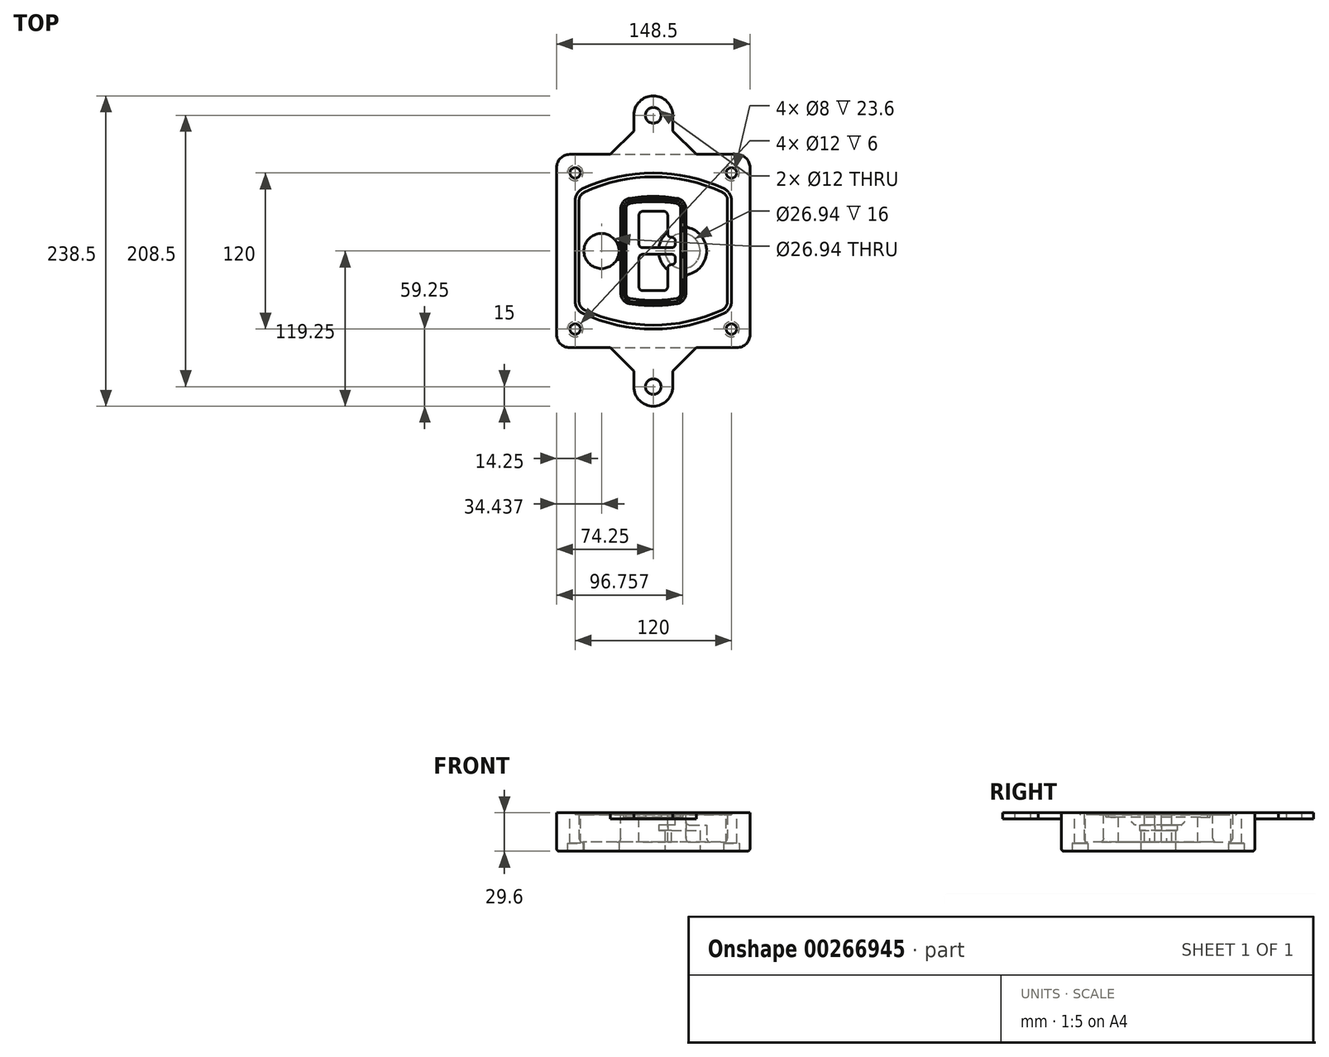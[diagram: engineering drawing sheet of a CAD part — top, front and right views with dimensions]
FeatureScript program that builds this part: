
annotation { "Feature Type Name" : "Feature", "Feature Type Description" : "" }
export const myFeature = defineFeature(function(context is Context, id is Id, definition is map)
    precondition{}
    {
        {
            var Q0;
            Q0=qCreatedBy(makeId("Top.planeOp"),FACE);
            var sketch = newSketch(context, id + "F0", { "sketchPlane" : qUnion([Q0])});
            skPoint(sketch, "E0.rect.middle", {"position": v(0, 0) * mm});
            skLineSegment(sketch, "E1.bottom", {"start": v(-64.25, -74.25) * mm, "end": v(64.25, -74.25) * mm});
            skLineSegment(sketch, "E1.top", {"start": v(-64.25, 74.25) * mm, "end": v(64.25, 74.25) * mm});
            skLineSegment(sketch, "E1.left", {"start": v(-74.25, -64.25) * mm, "end": v(-74.25, 64.25) * mm});
            skLineSegment(sketch, "E1.right", {"start": v(74.25, -64.25) * mm, "end": v(74.25, 64.25) * mm});
            skLineSegment(sketch, "E2", {"start": v(-74.25, 74.25) * mm, "end": v(74.25, -74.25) * mm, "construction": true});
            skLineSegment(sketch, "E3", {"start": v(74.25, 74.25) * mm, "end": v(-74.25, -74.25) * mm, "construction": true});
            skCircle(sketch, "E4", {"center": v(-60, 60) * mm, "radius": 4 * mm});
            skCircle(sketch, "E5", {"center": v(60, 60) * mm, "radius": 4 * mm});
            skCircle(sketch, "E6", {"center": v(60, -60) * mm, "radius": 4 * mm});
            skCircle(sketch, "E7", {"center": v(-60, -60) * mm, "radius": 4 * mm});
            skLineSegment(sketch, "E8", {"start": v(-60, 60) * mm, "end": v(60, 60) * mm, "construction": true});
            skLineSegment(sketch, "E9", {"start": v(60, 60) * mm, "end": v(60, -60) * mm, "construction": true});
            skLineSegment(sketch, "E10", {"start": v(60, -60) * mm, "end": v(-60, -60) * mm, "construction": true});
            skLineSegment(sketch, "E11", {"start": v(-60, -60) * mm, "end": v(-60, 60) * mm, "construction": true});
            skLineSegment(sketch, "E12", {"start": v(-60, 38.83) * mm, "end": v(-60, -38.83) * mm});
            skLineSegment(sketch, "E13", {"start": v(60, 38.83) * mm, "end": v(60, -38.83) * mm});
            skArc(sketch, "E14", {"start": v(54.26, 47.88) * mm, "mid": v(0, 60) * mm, "end": v(-54.26, 47.88) * mm});
            skArc(sketch, "E15", {"start": v(-54.26, -47.88) * mm, "mid": v(0, -60) * mm, "end": v(54.26, -47.88) * mm});
            skLineSegment(sketch, "E16", {"start": v(-60, 0) * mm, "end": v(60, 0) * mm, "construction": true});
            skPoint(sketch, "E17.visualSharp", {"position": v(-60, -45) * mm});
            skArc(sketch, "E17.filletArc", {"start": v(-60, -38.83) * mm, "mid": v(-58.44, -44.2) * mm, "end": v(-54.26, -47.88) * mm});
            skPoint(sketch, "E18.visualSharp", {"position": v(-60, 45) * mm});
            skArc(sketch, "E18.filletArc", {"start": v(-54.26, 47.88) * mm, "mid": v(-58.44, 44.2) * mm, "end": v(-60, 38.83) * mm});
            skPoint(sketch, "E19.visualSharp", {"position": v(60, 45) * mm});
            skArc(sketch, "E19.filletArc", {"start": v(60, 38.83) * mm, "mid": v(58.44, 44.2) * mm, "end": v(54.26, 47.88) * mm});
            skPoint(sketch, "E20.visualSharp", {"position": v(60, -45) * mm});
            skArc(sketch, "E20.filletArc", {"start": v(54.26, -47.88) * mm, "mid": v(58.44, -44.2) * mm, "end": v(60, -38.83) * mm});
            skPoint(sketch, "E21.visualSharp", {"position": v(-74.25, 74.25) * mm});
            skArc(sketch, "E21.filletArc", {"start": v(-64.25, 74.25) * mm, "mid": v(-71.32, 71.32) * mm, "end": v(-74.25, 64.25) * mm});
            skPoint(sketch, "E22.visualSharp", {"position": v(74.25, 74.25) * mm});
            skArc(sketch, "E22.filletArc", {"start": v(74.25, 64.25) * mm, "mid": v(71.32, 71.32) * mm, "end": v(64.25, 74.25) * mm});
            skPoint(sketch, "E23.visualSharp", {"position": v(74.25, -74.25) * mm});
            skArc(sketch, "E23.filletArc", {"start": v(64.25, -74.25) * mm, "mid": v(71.32, -71.32) * mm, "end": v(74.25, -64.25) * mm});
            skPoint(sketch, "E24.visualSharp", {"position": v(-74.25, -74.25) * mm});
            skArc(sketch, "E24.filletArc", {"start": v(-74.25, -64.25) * mm, "mid": v(-71.32, -71.32) * mm, "end": v(-64.25, -74.25) * mm});
            skArc(sketch, "E25.0", {"start": v(57, 38.83) * mm, "mid": v(55.9, 42.58) * mm, "end": v(52.98, 45.17) * mm});
            skLineSegment(sketch, "E25.1", {"start": v(57, 38.83) * mm, "end": v(57, -38.83) * mm});
            skArc(sketch, "E25.2", {"start": v(52.98, -45.17) * mm, "mid": v(55.9, -42.58) * mm, "end": v(57, -38.83) * mm});
            skArc(sketch, "E25.3", {"start": v(-52.98, -45.17) * mm, "mid": v(0, -57) * mm, "end": v(52.98, -45.17) * mm});
            skArc(sketch, "E25.4", {"start": v(-57, -38.83) * mm, "mid": v(-55.9, -42.58) * mm, "end": v(-52.98, -45.17) * mm});
            skArc(sketch, "E25.5", {"start": v(52.98, 45.17) * mm, "mid": v(0, 57) * mm, "end": v(-52.98, 45.17) * mm});
            skLineSegment(sketch, "E25.6", {"start": v(-57, 38.83) * mm, "end": v(-57, -38.83) * mm});
            skArc(sketch, "E25.7", {"start": v(-52.98, 45.17) * mm, "mid": v(-55.9, 42.58) * mm, "end": v(-57, 38.83) * mm});
            skArc(sketch, "E26.0", {"start": v(-55.96, 51.5) * mm, "mid": v(-61.82, 46.33) * mm, "end": v(-64, 38.83) * mm});
            skArc(sketch, "E26.1", {"start": v(55.96, 51.5) * mm, "mid": v(0, 64) * mm, "end": v(-55.96, 51.5) * mm});
            skArc(sketch, "E26.2", {"start": v(64, 38.83) * mm, "mid": v(61.82, 46.33) * mm, "end": v(55.96, 51.5) * mm});
            skLineSegment(sketch, "E26.3", {"start": v(64, 38.83) * mm, "end": v(64, -38.83) * mm});
            skArc(sketch, "E26.4", {"start": v(55.96, -51.5) * mm, "mid": v(61.82, -46.33) * mm, "end": v(64, -38.83) * mm});
            skLineSegment(sketch, "E26.5", {"start": v(-64, 38.83) * mm, "end": v(-64, -38.83) * mm});
            skArc(sketch, "E26.6", {"start": v(-55.96, -51.5) * mm, "mid": v(0, -64) * mm, "end": v(55.96, -51.5) * mm});
            skArc(sketch, "E26.7", {"start": v(-64, -38.83) * mm, "mid": v(-61.82, -46.33) * mm, "end": v(-55.96, -51.5) * mm});
            skSolve(sketch);
        }
        {
            var Q0;
            Q0=makeQuery(id+"F0.imprint","IMPRINT",FACE,{"disambiguationData":[TD([[makeQuery(id+"F0.imprint","IMPRINT",EDGE,{"derivedFrom":sQuery(id+"F0.wireOp",EDGE,"E1.bottom")}),1.0]])]});
            var Q1;
            Q1=makeQuery(id+"F0.imprint","IMPRINT",FACE,{"disambiguationData":[TD([[makeQuery(id+"F0.imprint","IMPRINT",EDGE,{"derivedFrom":sQuery(id+"F0.wireOp",EDGE,"E12")}),1.0]])]});
            var Q2;
            Q2=makeQuery(id+"F0.imprint","IMPRINT",FACE,{"disambiguationData":[TD([[makeQuery(id+"F0.imprint","IMPRINT",EDGE,{"derivedFrom":sQuery(id+"F0.wireOp",EDGE,"E25.0")}),1.0]])]});
            var Q3;
            Q3=makeQuery(id+"F0.imprint","IMPRINT",FACE,{"disambiguationData":[TD([[makeQuery(id+"F0.imprint","IMPRINT",EDGE,{"derivedFrom":sQuery(id+"F0.wireOp",EDGE,"E12")}),-1.0]])]});
            extrude(context, id + "F1", {"entities" : qUnion([Q0, Q1, Q2, Q3]), "oppositeDirection" : true, "depth" : 25 * mm});
        }
        {
            var Q0;
            Q0=makeQuery(id+"F0.imprint","IMPRINT",FACE,{"disambiguationData":[TD([[makeQuery(id+"F0.imprint","IMPRINT",EDGE,{"derivedFrom":sQuery(id+"F0.wireOp",EDGE,"E12")}),1.0]])]});
            extrude(context, id + "F2", {"entities" : qUnion([Q0]), "operationType" : NewBodyOperationType.ADD, "depth" : 3 * mm});
        }
        {
            var Q0;
            Q0=makeQuery(id+"F0.imprint","IMPRINT",FACE,{"disambiguationData":[TD([[makeQuery(id+"F0.imprint","IMPRINT",EDGE,{"derivedFrom":sQuery(id+"F0.wireOp",EDGE,"E25.0")}),1.0]])]});
            extrude(context, id + "F3", {"entities" : qUnion([Q0]), "operationType" : NewBodyOperationType.REMOVE, "oppositeDirection" : true, "depth" : 18 * mm});
        }
        {
            var Q0;
            Q0=makeQuery(id+"F2.opExtrude","CAP_FACE",FACE,{"disambiguationData":[OSD([sQuery(id+"F0.wireOp",EDGE,"E12"),sQuery(id+"F0.wireOp",EDGE,"E13"),sQuery(id+"F0.wireOp",EDGE,"E14"),sQuery(id+"F0.wireOp",EDGE,"E15"),sQuery(id+"F0.wireOp",EDGE,"E17.filletArc"),sQuery(id+"F0.wireOp",EDGE,"E18.filletArc"),sQuery(id+"F0.wireOp",EDGE,"E19.filletArc"),sQuery(id+"F0.wireOp",EDGE,"E20.filletArc"),sQuery(id+"F0.wireOp",EDGE,"E25.0"),sQuery(id+"F0.wireOp",EDGE,"E25.1"),sQuery(id+"F0.wireOp",EDGE,"E25.2"),sQuery(id+"F0.wireOp",EDGE,"E25.3"),sQuery(id+"F0.wireOp",EDGE,"E25.4"),sQuery(id+"F0.wireOp",EDGE,"E25.5"),sQuery(id+"F0.wireOp",EDGE,"E25.6"),sQuery(id+"F0.wireOp",EDGE,"E25.7")])],"isStart":false});
            var sketch = newSketch(context, id + "F4", { "sketchPlane" : qUnion([Q0])});
            skArc(sketch, "E27.0", {"start": v(-18.34, -40.45) * mm, "mid": v(0, -42) * mm, "end": v(18.34, -40.45) * mm});
            skArc(sketch, "E28.0", {"start": v(18.34, 40.45) * mm, "mid": v(0, 42) * mm, "end": v(-18.34, 40.45) * mm});
            skLineSegment(sketch, "E29", {"start": v(-25, 32.57) * mm, "end": v(-25, -32.57) * mm});
            skLineSegment(sketch, "E30", {"start": v(25, 32.57) * mm, "end": v(25, -32.57) * mm});
            skLineSegment(sketch, "E31", {"start": v(-25, 39.1) * mm, "end": v(25, 39.1) * mm, "construction": true});
            skLineSegment(sketch, "E32", {"start": v(-25, -39.1) * mm, "end": v(25, -39.1) * mm, "construction": true});
            skPoint(sketch, "E33.visualSharp", {"position": v(-25, 39.1) * mm});
            skArc(sketch, "E33.filletArc", {"start": v(-18.34, 40.45) * mm, "mid": v(-23.11, 37.73) * mm, "end": v(-25, 32.57) * mm});
            skPoint(sketch, "E34.visualSharp", {"position": v(25, 39.1) * mm});
            skArc(sketch, "E34.filletArc", {"start": v(25, 32.57) * mm, "mid": v(23.11, 37.73) * mm, "end": v(18.34, 40.45) * mm});
            skPoint(sketch, "E35.visualSharp", {"position": v(25, -39.1) * mm});
            skArc(sketch, "E35.filletArc", {"start": v(18.34, -40.45) * mm, "mid": v(23.11, -37.73) * mm, "end": v(25, -32.57) * mm});
            skPoint(sketch, "E36.visualSharp", {"position": v(-25, -39.1) * mm});
            skArc(sketch, "E36.filletArc", {"start": v(-25, -32.57) * mm, "mid": v(-23.11, -37.73) * mm, "end": v(-18.34, -40.45) * mm});
            skArc(sketch, "E37.0", {"start": v(52.98, 45.17) * mm, "mid": v(0, 57) * mm, "end": v(-52.98, 45.17) * mm});
            skArc(sketch, "E37.1", {"start": v(-52.98, 45.17) * mm, "mid": v(-55.9, 42.58) * mm, "end": v(-57, 38.83) * mm});
            skLineSegment(sketch, "E37.2", {"start": v(-57, 38.83) * mm, "end": v(-57, -38.83) * mm});
            skArc(sketch, "E37.3", {"start": v(-57, -38.83) * mm, "mid": v(-55.9, -42.58) * mm, "end": v(-52.98, -45.17) * mm});
            skArc(sketch, "E37.4", {"start": v(-52.98, -45.17) * mm, "mid": v(0, -57) * mm, "end": v(52.98, -45.17) * mm});
            skArc(sketch, "E37.5", {"start": v(52.98, -45.17) * mm, "mid": v(55.9, -42.58) * mm, "end": v(57, -38.83) * mm});
            skLineSegment(sketch, "E37.6", {"start": v(57, 38.83) * mm, "end": v(57, -38.83) * mm});
            skArc(sketch, "E37.7", {"start": v(57, 38.83) * mm, "mid": v(55.9, 42.58) * mm, "end": v(52.98, 45.17) * mm});
            skLineSegment(sketch, "E38.0", {"start": v(23, 32.57) * mm, "end": v(23, -32.57) * mm});
            skArc(sketch, "E38.1", {"start": v(18, -38.48) * mm, "mid": v(21.58, -36.44) * mm, "end": v(23, -32.57) * mm});
            skArc(sketch, "E38.2", {"start": v(-18, -38.48) * mm, "mid": v(0, -40) * mm, "end": v(18, -38.48) * mm});
            skArc(sketch, "E38.3", {"start": v(-23, -32.57) * mm, "mid": v(-21.58, -36.44) * mm, "end": v(-18, -38.48) * mm});
            skLineSegment(sketch, "E38.4", {"start": v(-23, 32.57) * mm, "end": v(-23, -32.57) * mm});
            skArc(sketch, "E38.5", {"start": v(23, 32.57) * mm, "mid": v(21.58, 36.44) * mm, "end": v(18, 38.48) * mm});
            skArc(sketch, "E38.6", {"start": v(-18, 38.48) * mm, "mid": v(-21.58, 36.44) * mm, "end": v(-23, 32.57) * mm});
            skArc(sketch, "E38.7", {"start": v(18, 38.48) * mm, "mid": v(0, 40) * mm, "end": v(-18, 38.48) * mm});
            skArc(sketch, "E39.0", {"start": v(21, 32.57) * mm, "mid": v(20.06, 35.15) * mm, "end": v(17.67, 36.5) * mm});
            skLineSegment(sketch, "E39.1", {"start": v(21, 32.57) * mm, "end": v(21, -32.57) * mm});
            skArc(sketch, "E39.2", {"start": v(17.67, -36.5) * mm, "mid": v(20.06, -35.15) * mm, "end": v(21, -32.57) * mm});
            skArc(sketch, "E39.3", {"start": v(-17.67, -36.5) * mm, "mid": v(0, -38) * mm, "end": v(17.67, -36.5) * mm});
            skArc(sketch, "E39.4", {"start": v(-21, -32.57) * mm, "mid": v(-20.06, -35.15) * mm, "end": v(-17.67, -36.5) * mm});
            skArc(sketch, "E39.5", {"start": v(17.67, 36.5) * mm, "mid": v(0, 38) * mm, "end": v(-17.67, 36.5) * mm});
            skLineSegment(sketch, "E39.6", {"start": v(-21, 32.57) * mm, "end": v(-21, -32.57) * mm});
            skArc(sketch, "E39.7", {"start": v(-17.67, 36.5) * mm, "mid": v(-20.06, 35.15) * mm, "end": v(-21, 32.57) * mm});
            skLineSegment(sketch, "E40", {"start": v(-25, 0) * mm, "end": v(25, 0) * mm, "construction": true});
            skLineSegment(sketch, "E41", {"start": v(-11, 5.5) * mm, "end": v(-11, 27.5) * mm});
            skLineSegment(sketch, "E42", {"start": v(-8, 30.5) * mm, "end": v(8, 30.5) * mm});
            skLineSegment(sketch, "E43", {"start": v(11, 27.5) * mm, "end": v(11, 13.5) * mm});
            skLineSegment(sketch, "E44", {"start": v(14, 10.5) * mm, "end": v(14, 10.5) * mm});
            skLineSegment(sketch, "E45", {"start": v(17, 7.5) * mm, "end": v(17, 5.5) * mm});
            skLineSegment(sketch, "E46", {"start": v(14, 2.5) * mm, "end": v(-8, 2.5) * mm});
            skPoint(sketch, "E47.visualSharp", {"position": v(-11, 30.5) * mm});
            skArc(sketch, "E47.filletArc", {"start": v(-8, 30.5) * mm, "mid": v(-10.12, 29.62) * mm, "end": v(-11, 27.5) * mm});
            skPoint(sketch, "E48.visualSharp", {"position": v(11, 30.5) * mm});
            skArc(sketch, "E48.filletArc", {"start": v(11, 27.5) * mm, "mid": v(10.12, 29.62) * mm, "end": v(8, 30.5) * mm});
            skPoint(sketch, "E49.visualSharp", {"position": v(11, 10.5) * mm});
            skArc(sketch, "E49.filletArc", {"start": v(11, 13.5) * mm, "mid": v(11.88, 11.38) * mm, "end": v(14, 10.5) * mm});
            skPoint(sketch, "E50.visualSharp", {"position": v(17, 10.5) * mm});
            skArc(sketch, "E50.filletArc", {"start": v(17, 7.5) * mm, "mid": v(16.12, 9.62) * mm, "end": v(14, 10.5) * mm});
            skPoint(sketch, "E51.visualSharp", {"position": v(17, 2.5) * mm});
            skArc(sketch, "E51.filletArc", {"start": v(14, 2.5) * mm, "mid": v(16.12, 3.38) * mm, "end": v(17, 5.5) * mm});
            skPoint(sketch, "E52.visualSharp", {"position": v(-11, 2.5) * mm});
            skArc(sketch, "E52.filletArc", {"start": v(-11, 5.5) * mm, "mid": v(-10.12, 3.38) * mm, "end": v(-8, 2.5) * mm});
            skLineSegment(sketch, "E53.0.MirrorCS", {"start": v(14, -2.5) * mm, "end": v(-8, -2.5) * mm});
            skArc(sketch, "E54.0.MirrorCS", {"start": v(-11, -5.5) * mm, "mid": v(-10.12, -3.38) * mm, "end": v(-8, -2.5) * mm});
            skLineSegment(sketch, "E55.0.MirrorCS", {"start": v(-11, -5.5) * mm, "end": v(-11, -27.5) * mm});
            skArc(sketch, "E56.0.MirrorCS", {"start": v(-8, -30.5) * mm, "mid": v(-10.12, -29.62) * mm, "end": v(-11, -27.5) * mm});
            skLineSegment(sketch, "E57.0.MirrorCS", {"start": v(-8, -30.5) * mm, "end": v(8, -30.5) * mm});
            skArc(sketch, "E58.0.MirrorCS", {"start": v(11, -27.5) * mm, "mid": v(10.12, -29.62) * mm, "end": v(8, -30.5) * mm});
            skLineSegment(sketch, "E59.0.MirrorCS", {"start": v(11, -27.5) * mm, "end": v(11, -13.5) * mm});
            skArc(sketch, "E60.0.MirrorCS", {"start": v(11, -13.5) * mm, "mid": v(11.88, -11.38) * mm, "end": v(14, -10.5) * mm});
            skArc(sketch, "E61.0.MirrorCS", {"start": v(17, -7.5) * mm, "mid": v(16.12, -9.62) * mm, "end": v(14, -10.5) * mm});
            skLineSegment(sketch, "E62.0.MirrorCS", {"start": v(17, -7.5) * mm, "end": v(17, -5.5) * mm});
            skArc(sketch, "E63.0.MirrorCS", {"start": v(14, -2.5) * mm, "mid": v(16.12, -3.38) * mm, "end": v(17, -5.5) * mm});
            skSolve(sketch);
        }
        {
            var Q0;
            Q0=makeQuery(id+"F4.imprint","IMPRINT",FACE,{"disambiguationData":[TD([[makeQuery(id+"F4.imprint","IMPRINT",EDGE,{"derivedFrom":sQuery(id+"F4.wireOp",EDGE,"E27.0")}),1.0]])]});
            var Q1;
            Q1=makeQuery(id+"F4.imprint","IMPRINT",FACE,{"disambiguationData":[TD([[makeQuery(id+"F4.imprint","IMPRINT",EDGE,{"derivedFrom":sQuery(id+"F4.wireOp",EDGE,"E38.0")}),-1.0]])]});
            var Q2;
            Q2=makeQuery(id+"F4.imprint","IMPRINT",FACE,{"disambiguationData":[TD([[makeQuery(id+"F4.imprint","IMPRINT",EDGE,{"derivedFrom":sQuery(id+"F4.wireOp",EDGE,"E39.0")}),1.0]])]});
            extrude(context, id + "F5", {"entities" : qUnion([Q0, Q1, Q2]), "operationType" : NewBodyOperationType.ADD, "endBound" : BoundingType.UP_TO_NEXT, "oppositeDirection" : true, "depth" : 25 * mm});
        }
        {
            var Q0;
            Q0=makeQuery(id+"F4.imprint","IMPRINT",FACE,{"disambiguationData":[TD([[makeQuery(id+"F4.imprint","IMPRINT",EDGE,{"derivedFrom":sQuery(id+"F4.wireOp",EDGE,"E38.0")}),-1.0]])]});
            extrude(context, id + "F6", {"entities" : qUnion([Q0]), "operationType" : NewBodyOperationType.REMOVE, "oppositeDirection" : true, "depth" : 2 * mm});
        }
        {
            var Q0;
            Q0=makeQuery(id+"F1.opExtrude","CAP_FACE",FACE,{"disambiguationData":[OSD([sQuery(id+"F0.wireOp",EDGE,"E1.bottom"),sQuery(id+"F0.wireOp",EDGE,"E1.top"),sQuery(id+"F0.wireOp",EDGE,"E1.left"),sQuery(id+"F0.wireOp",EDGE,"E1.right"),sQuery(id+"F0.wireOp",EDGE,"E4"),sQuery(id+"F0.wireOp",EDGE,"E5"),sQuery(id+"F0.wireOp",EDGE,"E6"),sQuery(id+"F0.wireOp",EDGE,"E7"),sQuery(id+"F0.wireOp",EDGE,"E21.filletArc"),sQuery(id+"F0.wireOp",EDGE,"E22.filletArc"),sQuery(id+"F0.wireOp",EDGE,"E23.filletArc"),sQuery(id+"F0.wireOp",EDGE,"E24.filletArc")])],"isStart":false});
            var sketch = newSketch(context, id + "F7", { "sketchPlane" : qUnion([Q0])});
            skCircle(sketch, "E64", {"center": v(22.5, 0) * mm, "radius": 13.47 * mm});
            skCircle(sketch, "E65", {"center": v(-39.81, 0) * mm, "radius": 13.47 * mm});
            skLineSegment(sketch, "E66", {"start": v(74.25, 0) * mm, "end": v(-74.25, 0) * mm});
            skCircle(sketch, "E67", {"center": v(22.5, 0) * mm, "radius": 18.47 * mm});
            skCircle(sketch, "E68", {"center": v(60, -60) * mm, "radius": 6 * mm});
            skCircle(sketch, "E69", {"center": v(-60, -60) * mm, "radius": 6 * mm});
            skCircle(sketch, "E70", {"center": v(-60, 60) * mm, "radius": 6 * mm});
            skCircle(sketch, "E71", {"center": v(60, 60) * mm, "radius": 6 * mm});
            skSolve(sketch);
        }
        {
            var Q0;
            {var subQ1=sQuery(id+"F7.wireOp",EDGE,"E66");var subQ4=sQuery(id+"F7.wireOp",EDGE,"E64");var subQ6=makeQuery(id+"F7.imprint","INTERSECT",VERTEX,{"disambiguationData":[OD(0.0)],"derivedFrom":[subQ4,subQ1]});Q0=makeQuery(id+"F7.imprint","IMPRINT",FACE,{"disambiguationData":[TD([[makeQuery(id+"F7.imprint","IMPRINT",EDGE,{"disambiguationData":[TD([[subQ6,-1.0]])],"derivedFrom":subQ4}),-1.0]])]});}
            var Q1;
            {var subQ0=sQuery(id+"F7.wireOp",EDGE,"E66");var subQ1=sQuery(id+"F7.wireOp",EDGE,"E64");var subQ3=makeQuery(id+"F7.imprint","INTERSECT",VERTEX,{"disambiguationData":[OD(0.0)],"derivedFrom":[subQ1,subQ0]});Q1=makeQuery(id+"F7.imprint","IMPRINT",FACE,{"disambiguationData":[TD([[makeQuery(id+"F7.imprint","IMPRINT",EDGE,{"disambiguationData":[TD([[subQ3,-1.0]])],"derivedFrom":subQ1}),1.0]])]});}
            var Q2;
            {var subQ0=sQuery(id+"F7.wireOp",EDGE,"E66");var subQ1=sQuery(id+"F7.wireOp",EDGE,"E64");var subQ3=makeQuery(id+"F7.imprint","INTERSECT",VERTEX,{"disambiguationData":[OD(0.0)],"derivedFrom":[subQ1,subQ0]});Q2=makeQuery(id+"F7.imprint","IMPRINT",FACE,{"disambiguationData":[TD([[makeQuery(id+"F7.imprint","IMPRINT",EDGE,{"disambiguationData":[TD([[subQ3,1.0]])],"derivedFrom":subQ1}),1.0]])]});}
            var Q3;
            {var subQ1=sQuery(id+"F7.wireOp",EDGE,"E66");var subQ4=sQuery(id+"F7.wireOp",EDGE,"E64");var subQ6=makeQuery(id+"F7.imprint","INTERSECT",VERTEX,{"disambiguationData":[OD(0.0)],"derivedFrom":[subQ4,subQ1]});Q3=makeQuery(id+"F7.imprint","IMPRINT",FACE,{"disambiguationData":[TD([[makeQuery(id+"F7.imprint","IMPRINT",EDGE,{"disambiguationData":[TD([[subQ6,1.0]])],"derivedFrom":subQ4}),-1.0]])]});}
            extrude(context, id + "F8", {"entities" : qUnion([Q0, Q1, Q2, Q3]), "operationType" : NewBodyOperationType.ADD, "oppositeDirection" : true, "depth" : 20 * mm});
        }
        {
            var Q0;
            {var subQ0=sQuery(id+"F7.wireOp",EDGE,"E66");var subQ1=sQuery(id+"F7.wireOp",EDGE,"E64");var subQ3=makeQuery(id+"F7.imprint","INTERSECT",VERTEX,{"disambiguationData":[OD(0.0)],"derivedFrom":[subQ1,subQ0]});Q0=makeQuery(id+"F7.imprint","IMPRINT",FACE,{"disambiguationData":[TD([[makeQuery(id+"F7.imprint","IMPRINT",EDGE,{"disambiguationData":[TD([[subQ3,-1.0]])],"derivedFrom":subQ1}),1.0]])]});}
            var Q1;
            {var subQ0=sQuery(id+"F7.wireOp",EDGE,"E66");var subQ1=sQuery(id+"F7.wireOp",EDGE,"E64");var subQ3=makeQuery(id+"F7.imprint","INTERSECT",VERTEX,{"disambiguationData":[OD(0.0)],"derivedFrom":[subQ1,subQ0]});Q1=makeQuery(id+"F7.imprint","IMPRINT",FACE,{"disambiguationData":[TD([[makeQuery(id+"F7.imprint","IMPRINT",EDGE,{"disambiguationData":[TD([[subQ3,1.0]])],"derivedFrom":subQ1}),1.0]])]});}
            extrude(context, id + "F9", {"entities" : qUnion([Q0, Q1]), "operationType" : NewBodyOperationType.REMOVE, "oppositeDirection" : true, "depth" : 16 * mm});
        }
        {
            var Q0;
            {var subQ0=sQuery(id+"F7.wireOp",EDGE,"E66");var subQ1=sQuery(id+"F7.wireOp",EDGE,"E65");var subQ3=makeQuery(id+"F7.imprint","INTERSECT",VERTEX,{"disambiguationData":[OD(0.0)],"derivedFrom":[subQ1,subQ0]});Q0=makeQuery(id+"F7.imprint","IMPRINT",FACE,{"disambiguationData":[TD([[makeQuery(id+"F7.imprint","IMPRINT",EDGE,{"disambiguationData":[TD([[subQ3,-1.0]])],"derivedFrom":subQ1}),1.0]])]});}
            var Q1;
            {var subQ0=sQuery(id+"F7.wireOp",EDGE,"E66");var subQ1=sQuery(id+"F7.wireOp",EDGE,"E65");var subQ3=makeQuery(id+"F7.imprint","INTERSECT",VERTEX,{"disambiguationData":[OD(0.0)],"derivedFrom":[subQ1,subQ0]});Q1=makeQuery(id+"F7.imprint","IMPRINT",FACE,{"disambiguationData":[TD([[makeQuery(id+"F7.imprint","IMPRINT",EDGE,{"disambiguationData":[TD([[subQ3,1.0]])],"derivedFrom":subQ1}),1.0]])]});}
            extrude(context, id + "F10", {"entities" : qUnion([Q0, Q1]), "operationType" : NewBodyOperationType.REMOVE, "oppositeDirection" : true, "depth" : 25 * mm});
        }
        {
            var Q0;
            Q0=makeQuery(id+"F7.imprint","IMPRINT",FACE,{"disambiguationData":[TD([[makeQuery(id+"F7.imprint","IMPRINT",EDGE,{"derivedFrom":sQuery(id+"F7.wireOp",EDGE,"E68")}),1.0]])]});
            var Q1;
            Q1=makeQuery(id+"F7.imprint","IMPRINT",FACE,{"disambiguationData":[TD([[makeQuery(id+"F7.imprint","IMPRINT",EDGE,{"derivedFrom":makeQuery(id+"F1.opExtrude","CAP_EDGE",EDGE,{"disambiguationData":[OSD([sQuery(id+"F0.wireOp",EDGE,"E5")])],"isStart":false})}),-1.0]])]});
            var Q2;
            Q2=makeQuery(id+"F7.imprint","IMPRINT",FACE,{"disambiguationData":[TD([[makeQuery(id+"F7.imprint","IMPRINT",EDGE,{"derivedFrom":sQuery(id+"F7.wireOp",EDGE,"E69")}),1.0]])]});
            var Q3;
            Q3=makeQuery(id+"F7.imprint","IMPRINT",FACE,{"disambiguationData":[TD([[makeQuery(id+"F7.imprint","IMPRINT",EDGE,{"derivedFrom":makeQuery(id+"F1.opExtrude","CAP_EDGE",EDGE,{"disambiguationData":[OSD([sQuery(id+"F0.wireOp",EDGE,"E4")])],"isStart":false})}),-1.0]])]});
            var Q4;
            Q4=makeQuery(id+"F7.imprint","IMPRINT",FACE,{"disambiguationData":[TD([[makeQuery(id+"F7.imprint","IMPRINT",EDGE,{"derivedFrom":sQuery(id+"F7.wireOp",EDGE,"E70")}),1.0]])]});
            var Q5;
            Q5=makeQuery(id+"F7.imprint","IMPRINT",FACE,{"disambiguationData":[TD([[makeQuery(id+"F7.imprint","IMPRINT",EDGE,{"derivedFrom":makeQuery(id+"F1.opExtrude","CAP_EDGE",EDGE,{"disambiguationData":[OSD([sQuery(id+"F0.wireOp",EDGE,"E7")])],"isStart":false})}),-1.0]])]});
            var Q6;
            Q6=makeQuery(id+"F7.imprint","IMPRINT",FACE,{"disambiguationData":[TD([[makeQuery(id+"F7.imprint","IMPRINT",EDGE,{"derivedFrom":sQuery(id+"F7.wireOp",EDGE,"E71")}),1.0]])]});
            var Q7;
            Q7=makeQuery(id+"F7.imprint","IMPRINT",FACE,{"disambiguationData":[TD([[makeQuery(id+"F7.imprint","IMPRINT",EDGE,{"derivedFrom":makeQuery(id+"F1.opExtrude","CAP_EDGE",EDGE,{"disambiguationData":[OSD([sQuery(id+"F0.wireOp",EDGE,"E6")])],"isStart":false})}),-1.0]])]});
            extrude(context, id + "F11", {"entities" : qUnion([Q0, Q1, Q2, Q3, Q4, Q5, Q6, Q7]), "operationType" : NewBodyOperationType.REMOVE, "oppositeDirection" : true, "depth" : 6 * mm});
        }
        {
            var Q0;
            Q0=makeQuery(id+"F9.boolean.opBoolean","COPY",FACE,{"derivedFrom":makeQuery(id+"F9.opExtrude","CAP_FACE",FACE,{"disambiguationData":[OSD([sQuery(id+"F7.wireOp",EDGE,"E64")])],"isStart":false})});
            var sketch = newSketch(context, id + "F12", { "sketchPlane" : qUnion([Q0])});
            skArc(sketch, "E72.0", {"start": v(11, 14.45) * mm, "mid": v(6.45, 9.13) * mm, "end": v(4.2, 2.5) * mm});
            skArc(sketch, "E72.1", {"start": v(4.2, -2.5) * mm, "mid": v(6.45, -9.13) * mm, "end": v(11, -14.45) * mm});
            skLineSegment(sketch, "E73", {"start": v(4.2, -2.5) * mm, "end": v(14, -2.5) * mm});
            skLineSegment(sketch, "E74.0", {"start": v(14, 2.5) * mm, "end": v(4.2, 2.5) * mm});
            skArc(sketch, "E74.1", {"start": v(14, 2.5) * mm, "mid": v(16.12, 3.38) * mm, "end": v(17, 5.5) * mm});
            skLineSegment(sketch, "E74.2", {"start": v(17, 7.5) * mm, "end": v(17, 5.5) * mm});
            skArc(sketch, "E74.3", {"start": v(17, 7.5) * mm, "mid": v(16.12, 9.62) * mm, "end": v(14, 10.5) * mm});
            skArc(sketch, "E74.4", {"start": v(11, 13.5) * mm, "mid": v(11.88, 11.38) * mm, "end": v(14, 10.5) * mm});
            skLineSegment(sketch, "E74.5", {"start": v(11, 14.45) * mm, "end": v(11, 13.5) * mm});
            skLineSegment(sketch, "E74.7", {"start": v(14, -2.5) * mm, "end": v(4.2, -2.5) * mm});
            skArc(sketch, "E74.8", {"start": v(14, -2.5) * mm, "mid": v(16.12, -3.38) * mm, "end": v(17, -5.5) * mm});
            skLineSegment(sketch, "E74.9", {"start": v(17, -7.5) * mm, "end": v(17, -5.5) * mm});
            skArc(sketch, "E74.10", {"start": v(17, -7.5) * mm, "mid": v(16.12, -9.62) * mm, "end": v(14, -10.5) * mm});
            skArc(sketch, "E74.11", {"start": v(11, -13.5) * mm, "mid": v(11.88, -11.38) * mm, "end": v(14, -10.5) * mm});
            skLineSegment(sketch, "E74.12", {"start": v(11, -14.45) * mm, "end": v(11, -13.5) * mm});
            skPoint(sketch, "E75.orphan", {"position": v(11, -27.5) * mm});
            skPoint(sketch, "E76.orphan", {"position": v(-8, -2.5) * mm});
            skPoint(sketch, "E77.orphan", {"position": v(-8, 2.5) * mm});
            skPoint(sketch, "E78.orphan", {"position": v(11, 27.5) * mm});
            skSolve(sketch);
        }
        {
            var Q0;
            {var subQ7=sQuery(id+"F12.wireOp",EDGE,"E72.0");var subQ14=sQuery(id+"F12.wireOp",EDGE,"E72.1");var subQ16=sQuery(id+"F12.wireOp",EDGE,"E74.1");var subQ18=sQuery(id+"F12.wireOp",EDGE,"E74.8");Q0=qUnion([makeQuery(id+"F12.imprint","IMPRINT",FACE,{"disambiguationData":[TD([[makeQuery(id+"F12.imprint","IMPRINT",EDGE,{"derivedFrom":subQ7}),1.0]])]}),makeQuery(id+"F12.imprint","IMPRINT",FACE,{"disambiguationData":[TD([[makeQuery(id+"F12.imprint","IMPRINT",EDGE,{"derivedFrom":subQ14}),1.0]])]}),makeQuery(id+"F12.imprint","IMPRINT",FACE,{"disambiguationData":[TD([[makeQuery(id+"F12.imprint","IMPRINT",EDGE,{"derivedFrom":subQ16}),1.0]])]}),makeQuery(id+"F12.imprint","IMPRINT",FACE,{"disambiguationData":[TD([[makeQuery(id+"F12.imprint","IMPRINT",EDGE,{"derivedFrom":subQ18}),-1.0]])]})]);}
            var Q1;
            Q1=makeQuery(id+"F5.boolean.opBoolean","SPLIT",FACE,{"disambiguationData":[TD([makeQuery(id+"F5.opExtrude","SWEPT_FACE",FACE,{"disambiguationData":[OSD([sQuery(id+"F4.wireOp",EDGE,"E41")])]})])],"derivedFrom":makeQuery(id+"F3.boolean.opBoolean","COPY",FACE,{"derivedFrom":makeQuery(id+"F3.opExtrude","CAP_FACE",FACE,{"disambiguationData":[OSD([sQuery(id+"F0.wireOp",EDGE,"E25.0"),sQuery(id+"F0.wireOp",EDGE,"E25.1"),sQuery(id+"F0.wireOp",EDGE,"E25.2"),sQuery(id+"F0.wireOp",EDGE,"E25.3"),sQuery(id+"F0.wireOp",EDGE,"E25.4"),sQuery(id+"F0.wireOp",EDGE,"E25.5"),sQuery(id+"F0.wireOp",EDGE,"E25.6"),sQuery(id+"F0.wireOp",EDGE,"E25.7")])],"isStart":false})})});
            extrude(context, id + "F13", {"entities" : qUnion([Q0]), "operationType" : NewBodyOperationType.REMOVE, "endBound" : BoundingType.UP_TO_SURFACE, "endBoundEntityFace" : qUnion([Q1]), "depth" : 25 * mm});
        }
        {
            var Q0;
            Q0=makeQuery(id+"F3.boolean.opBoolean","COPY",EDGE,{"derivedFrom":makeQuery(id+"F3.opExtrude","CAP_EDGE",EDGE,{"disambiguationData":[OSD([sQuery(id+"F0.wireOp",EDGE,"E25.6")])],"isStart":false})});
            var Q1;
            Q1=makeQuery(id+"F8.boolean.opBoolean","INTERSECT",EDGE,{"derivedFrom":[makeQuery(id+"F5.opExtrude","SWEPT_FACE",FACE,{"disambiguationData":[OSD([sQuery(id+"F4.wireOp",EDGE,"E30")])]}),makeQuery(id+"F8.opExtrude","CAP_FACE",FACE,{"disambiguationData":[OSD([sQuery(id+"F7.wireOp",EDGE,"E67")])],"isStart":false})]});
            var Q2;
            Q2=makeQuery(id+"F8.boolean.opBoolean","INTERSECT",EDGE,{"disambiguationData":[OD(1.0)],"derivedFrom":[makeQuery(id+"F5.opExtrude","SWEPT_FACE",FACE,{"disambiguationData":[OSD([sQuery(id+"F4.wireOp",EDGE,"E30")])]}),makeQuery(id+"F8.opExtrude","SWEPT_FACE",FACE,{"disambiguationData":[OSD([sQuery(id+"F7.wireOp",EDGE,"E67")])]})]});
            var Q3;
            {var subQ0=sQuery(id+"F4.wireOp",EDGE,"E30");Q3=makeQuery(id+"F8.boolean.opBoolean","SPLIT",EDGE,{"disambiguationData":[TD([makeQuery(id+"F5.opExtrude","SWEPT_FACE",FACE,{"disambiguationData":[OSD([sQuery(id+"F4.wireOp",EDGE,"E35.filletArc")])]})])],"derivedFrom":makeQuery(id+"F5.opExtrude","CAP_EDGE",EDGE,{"disambiguationData":[OSD([subQ0])],"isStart":false})});}
            var Q4;
            {var subQ0=sQuery(id+"F0.wireOp",EDGE,"E25.7");var subQ1=sQuery(id+"F0.wireOp",EDGE,"E25.1");var subQ2=sQuery(id+"F0.wireOp",EDGE,"E25.6");var subQ3=sQuery(id+"F0.wireOp",EDGE,"E25.5");var subQ4=sQuery(id+"F0.wireOp",EDGE,"E25.4");var subQ5=sQuery(id+"F0.wireOp",EDGE,"E25.0");var subQ6=sQuery(id+"F0.wireOp",EDGE,"E25.2");var subQ7=sQuery(id+"F0.wireOp",EDGE,"E25.3");Q4=makeQuery(id+"F8.boolean.opBoolean","INTERSECT",EDGE,{"derivedFrom":[makeQuery(id+"F5.boolean.opBoolean","SPLIT",FACE,{"disambiguationData":[TD([makeQuery(id+"F2.opExtrude","SWEPT_FACE",FACE,{"disambiguationData":[OSD([subQ5])]})])],"derivedFrom":makeQuery(id+"F3.boolean.opBoolean","COPY",FACE,{"derivedFrom":makeQuery(id+"F3.opExtrude","CAP_FACE",FACE,{"disambiguationData":[OSD([subQ5,subQ1,subQ6,subQ7,subQ4,subQ3,subQ2,subQ0])],"isStart":false})})}),makeQuery(id+"F8.opExtrude","SWEPT_FACE",FACE,{"disambiguationData":[OSD([sQuery(id+"F7.wireOp",EDGE,"E67")])]})]});}
            var Q5;
            Q5=makeQuery(id+"F8.boolean.opBoolean","INTERSECT",EDGE,{"disambiguationData":[OD(0.0)],"derivedFrom":[makeQuery(id+"F5.opExtrude","SWEPT_FACE",FACE,{"disambiguationData":[OSD([sQuery(id+"F4.wireOp",EDGE,"E30")])]}),makeQuery(id+"F8.opExtrude","SWEPT_FACE",FACE,{"disambiguationData":[OSD([sQuery(id+"F7.wireOp",EDGE,"E67")])]})]});
            fillet(context, id + "F14", {"entities" : qUnion([Q0, Q1, Q2, Q3, Q4, Q5]), "radius" : 3 * mm, "tangentPropagation" : true, "allowEdgeOverflow" : false});
        }
        {
            var Q0;
            Q0=makeQuery(id+"F1.opExtrude","CAP_EDGE",EDGE,{"disambiguationData":[OSD([sQuery(id+"F0.wireOp",EDGE,"E1.bottom")])],"isStart":false});
            fillet(context, id + "F15", {"entities" : qUnion([Q0]), "radius" : 2 * mm, "tangentPropagation" : true, "allowEdgeOverflow" : false});
        }
        {
            var Q0;
            {var subQ0=sQuery(id+"F0.wireOp",EDGE,"E22.filletArc");var subQ1=sQuery(id+"F0.wireOp",EDGE,"E7");var subQ2=sQuery(id+"F0.wireOp",EDGE,"E6");var subQ3=sQuery(id+"F0.wireOp",EDGE,"E5");var subQ4=sQuery(id+"F0.wireOp",EDGE,"E4");var subQ5=sQuery(id+"F0.wireOp",EDGE,"E1.bottom");var subQ6=sQuery(id+"F0.wireOp",EDGE,"E21.filletArc");var subQ7=sQuery(id+"F0.wireOp",EDGE,"E1.top");var subQ8=sQuery(id+"F0.wireOp",EDGE,"E1.left");var subQ9=sQuery(id+"F0.wireOp",EDGE,"E1.right");var subQ10=sQuery(id+"F0.wireOp",EDGE,"E23.filletArc");var subQ11=sQuery(id+"F0.wireOp",EDGE,"E24.filletArc");Q0=makeQuery(id+"F2.boolean.opBoolean","SPLIT",FACE,{"disambiguationData":[TD([makeQuery(id+"F1.opExtrude","SWEPT_FACE",FACE,{"disambiguationData":[OSD([subQ5])]})])],"derivedFrom":makeQuery(id+"F1.opExtrude","CAP_FACE",FACE,{"disambiguationData":[OSD([subQ5,subQ7,subQ8,subQ9,subQ4,subQ3,subQ2,subQ1,subQ6,subQ0,subQ10,subQ11])],"isStart":true})});}
            var sketch = newSketch(context, id + "F16", { "sketchPlane" : qUnion([Q0])});
            skLineSegment(sketch, "E79", {"start": v(0, 74.25) * mm, "end": v(0, 104.25) * mm, "construction": true});
            skCircle(sketch, "E80", {"center": v(0, 104.25) * mm, "radius": 6 * mm});
            skArc(sketch, "E81", {"start": v(15, 104.25) * mm, "mid": v(0, 119.25) * mm, "end": v(-15, 104.25) * mm});
            skLineSegment(sketch, "E82", {"start": v(-15, 104.25) * mm, "end": v(-15, 92.25) * mm});
            skLineSegment(sketch, "E83", {"start": v(-15, 92.25) * mm, "end": v(-33, 74.25) * mm});
            skLineSegment(sketch, "E84", {"start": v(15, 104.25) * mm, "end": v(15, 92.25) * mm});
            skLineSegment(sketch, "E85", {"start": v(15, 92.25) * mm, "end": v(33, 74.25) * mm});
            skLineSegment(sketch, "E86", {"start": v(-74.25, 0) * mm, "end": v(74.25, 0) * mm, "construction": true});
            skLineSegment(sketch, "E87.MirrorCS", {"start": v(15, -104.25) * mm, "end": v(15, -92.25) * mm});
            skLineSegment(sketch, "E88.MirrorCS", {"start": v(15, -92.25) * mm, "end": v(33, -74.25) * mm});
            skLineSegment(sketch, "E89.MirrorCS", {"start": v(0, -74.25) * mm, "end": v(0, -104.25) * mm, "construction": true});
            skArc(sketch, "E90.MirrorCS", {"start": v(15, -104.25) * mm, "mid": v(0, -119.25) * mm, "end": v(-15, -104.25) * mm});
            skLineSegment(sketch, "E91.MirrorCS", {"start": v(-15, -104.25) * mm, "end": v(-15, -92.25) * mm});
            skCircle(sketch, "E92.MirrorC", {"center": v(0, -104.25) * mm, "radius": 6 * mm});
            skLineSegment(sketch, "E93.MirrorCS", {"start": v(-15, -92.25) * mm, "end": v(-33, -74.25) * mm});
            skSolve(sketch);
        }
        {
            var Q0;
            Q0=makeQuery(id+"F16.imprint","IMPRINT",FACE,{"disambiguationData":[TD([[makeQuery(id+"F16.imprint","IMPRINT",EDGE,{"derivedFrom":sQuery(id+"F16.wireOp",EDGE,"E87.MirrorCS")}),1.0]])]});
            var Q1;
            Q1=makeQuery(id+"F16.imprint","IMPRINT",FACE,{"disambiguationData":[TD([[makeQuery(id+"F16.imprint","IMPRINT",EDGE,{"derivedFrom":makeQuery(id+"F1.opExtrude","CAP_EDGE",EDGE,{"disambiguationData":[OSD([sQuery(id+"F0.wireOp",EDGE,"E1.left")])],"isStart":true})}),-1.0]])]});
            var Q2;
            Q2=makeQuery(id+"F16.imprint","IMPRINT",FACE,{"disambiguationData":[TD([[makeQuery(id+"F16.imprint","IMPRINT",EDGE,{"derivedFrom":sQuery(id+"F16.wireOp",EDGE,"E80")}),-1.0]])]});
            extrude(context, id + "F17", {"entities" : qUnion([Q0, Q1, Q2]), "operationType" : NewBodyOperationType.ADD, "depth" : 4.6 * mm});
        }
    });
